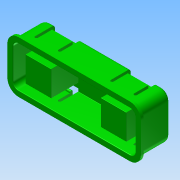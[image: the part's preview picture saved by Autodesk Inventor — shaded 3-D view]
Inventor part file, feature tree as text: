
AUTODESK INVENTOR PART (.ipt)
format: ipt  version: 2015 (Build 190159000, 159)  size: 285,696 bytes
history: native  units: in
note: dims shown in document units (in); Inventor stores cm internally (conversion verified against a paired STEP export)
features: fillet x6, extrude x4, sketch x3, shell x2, plane x2, mirror x2
ambient origin geometry x8: Origin, YZ Plane, XZ Plane, XY Plane, X Axis, Y Axis, Z Axis, Center Point
bodies: Solid1 (feature_tree)
feature tree (19):
  extrude  "Extrusion1"  Depth=0.465in
  fillet  "Fillet1"  Radius=0.57in
  shell  "Shell1"  Thickness=0.2in
  sketch  "Sketch2"  dims[d7=0.46in d8=0.2283in]
  plane  "Work Plane1"
  sketch  "Sketch3"  dims[d9=-0.033in d10=0.47in d11=0.0in d12=0.005in d13=0.01in d14=0.47in d15=0.05in d16=0.1in d17=0.05in d18=0.05in d19=0.15in d20=0.0in d21=0.125in d22=0.0in d23=0.05in d24=0.03in d26=0.445in d27=0.445in d28=0.05in]
  shell  "Shell2"  Thickness=0.1in
  extrude  "Extrusion3"  Depth=0.46in
  plane  "Work Plane2"
  extrude  "Extrusion4"  Depth=0.47in TaperAngle=0.0deg
  fillet  "Fillet6"  Radius=0.005in
  fillet  "Fillet3"  Radius=0.01in
  fillet  "Fillet4"  Radius=0.47in
  extrude  "Extrusion2"  Depth=0.05in
  fillet  "Fillet2"  Radius=0.1in
  fillet  "Fillet7"  Radius=0.05in
  mirror  "Mirror1"
  mirror  "Mirror2"
  sketch  "Sketch1"  dims[d0=1.2in d1=0.465in d2=0.57in d3=0.0in d4=0.2in d5=0.1in]
